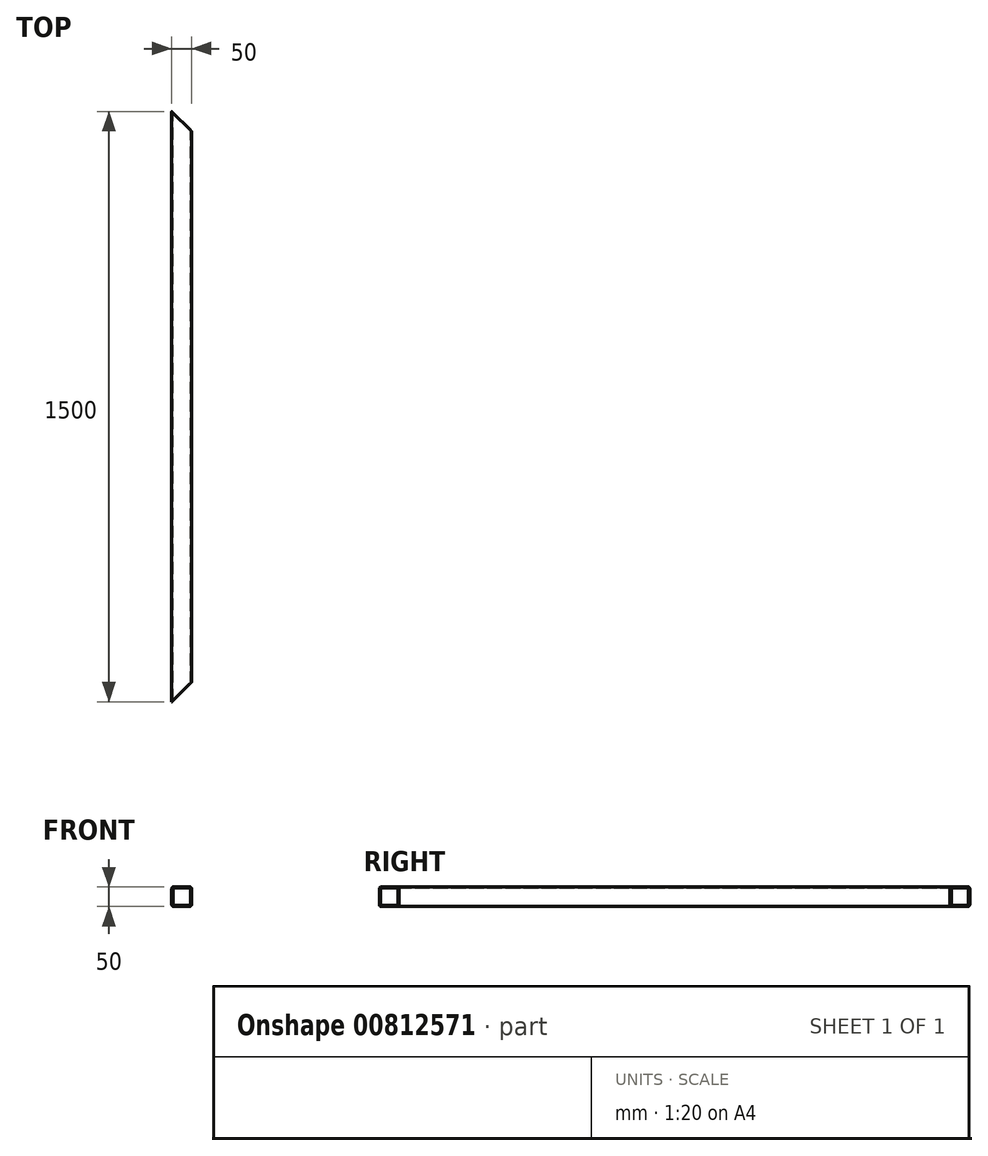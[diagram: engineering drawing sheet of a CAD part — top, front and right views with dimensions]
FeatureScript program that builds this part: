
annotation { "Feature Type Name" : "Feature", "Feature Type Description" : "" }
export const myFeature = defineFeature(function(context is Context, id is Id, definition is map)
    precondition{}
    {
        {
            var Q0;
            Q0=qCreatedBy(makeId("Front.planeOp"),FACE);
            var sketch = newSketch(context, id + "F0", { "sketchPlane" : qUnion([Q0])});
            skLineSegment(sketch, "E0.bottom", {"start": v(50, 50) * mm, "end": v(0, 50) * mm});
            skLineSegment(sketch, "E0.top", {"start": v(50, 0) * mm, "end": v(0, 0) * mm});
            skLineSegment(sketch, "E0.left", {"start": v(50, 50) * mm, "end": v(50, 0) * mm});
            skLineSegment(sketch, "E0.right", {"start": v(0, 50) * mm, "end": v(0, 0) * mm});
            skLineSegment(sketch, "E1.0", {"start": v(47, 3) * mm, "end": v(3, 3) * mm});
            skLineSegment(sketch, "E1.1", {"start": v(47, 47) * mm, "end": v(47, 3) * mm});
            skLineSegment(sketch, "E1.2", {"start": v(47, 47) * mm, "end": v(3, 47) * mm});
            skLineSegment(sketch, "E1.3", {"start": v(3, 47) * mm, "end": v(3, 3) * mm});
            skSolve(sketch);
        }
        {
            var Q0;
            Q0=qSketchRegion(id+"F0",true);
            extrude(context, id + "F1", {"entities" : qUnion([Q0]), "depth" : 1500 * mm, "offsetDistance" : 25 * mm});
        }
        {
            var Q0;
            Q0=qSketchRegion(id+"F0",true);
            extrude(context, id + "F2", {"entities" : qUnion([Q0]), "operationType" : NewBodyOperationType.ADD, "depth" : 100 * mm, "offsetDistance" : 25 * mm});
        }
        {
            var Q0;
            Q0=makeQuery(id+"F1.opExtrude","SWEPT_EDGE",EDGE,{"disambiguationData":[OSD([sQuery(id+"F0.wireOp",EDGE,"E0.bottom"),sQuery(id+"F0.wireOp",EDGE,"E0.left")])]});
            var Q1;
            Q1=makeQuery(id+"F1.opExtrude","SWEPT_EDGE",EDGE,{"disambiguationData":[OSD([sQuery(id+"F0.wireOp",EDGE,"E0.top"),sQuery(id+"F0.wireOp",EDGE,"E0.left")])]});
            var Q2;
            Q2=makeQuery(id+"F1.opExtrude","SWEPT_EDGE",EDGE,{"disambiguationData":[OSD([sQuery(id+"F0.wireOp",EDGE,"E0.top"),sQuery(id+"F0.wireOp",EDGE,"E0.right")])]});
            var Q3;
            Q3=makeQuery(id+"F1.opExtrude","SWEPT_EDGE",EDGE,{"disambiguationData":[OSD([sQuery(id+"F0.wireOp",EDGE,"E0.bottom"),sQuery(id+"F0.wireOp",EDGE,"E0.right")])]});
            fillet(context, id + "F3", {"entities" : qUnion([Q0, Q1, Q2, Q3]), "radius" : 5 * mm, "tangentPropagation" : true, "allowEdgeOverflow" : false});
        }
        {
            var Q0;
            Q0=makeQuery(id+"F1.opExtrude","SWEPT_EDGE",EDGE,{"disambiguationData":[OSD([sQuery(id+"F0.wireOp",EDGE,"E1.1"),sQuery(id+"F0.wireOp",EDGE,"E1.2")])]});
            var Q1;
            Q1=makeQuery(id+"F1.opExtrude","SWEPT_EDGE",EDGE,{"disambiguationData":[OSD([sQuery(id+"F0.wireOp",EDGE,"E1.0"),sQuery(id+"F0.wireOp",EDGE,"E1.3")])]});
            var Q2;
            Q2=makeQuery(id+"F1.opExtrude","SWEPT_EDGE",EDGE,{"disambiguationData":[OSD([sQuery(id+"F0.wireOp",EDGE,"E1.2"),sQuery(id+"F0.wireOp",EDGE,"E1.3")])]});
            var Q3;
            Q3=makeQuery(id+"F1.opExtrude","SWEPT_EDGE",EDGE,{"disambiguationData":[OSD([sQuery(id+"F0.wireOp",EDGE,"E1.0"),sQuery(id+"F0.wireOp",EDGE,"E1.1")])]});
            fillet(context, id + "F4", {"entities" : qUnion([Q0, Q1, Q2, Q3]), "radius" : 3 * mm, "tangentPropagation" : true, "allowEdgeOverflow" : false});
        }
        {
            var Q0;
            Q0=makeQuery(id+"F1.opExtrude","SWEPT_FACE",FACE,{"disambiguationData":[OSD([sQuery(id+"F0.wireOp",EDGE,"E0.bottom")])]});
            var sketch = newSketch(context, id + "F5", { "sketchPlane" : qUnion([Q0])});
            skLineSegment(sketch, "E2", {"start": v(0, 0) * mm, "end": v(50, 0) * mm});
            skLineSegment(sketch, "E3", {"start": v(50, 0) * mm, "end": v(50, -50) * mm});
            skLineSegment(sketch, "E4", {"start": v(50, -50) * mm, "end": v(0, 0) * mm});
            skPoint(sketch, "E5.orphan", {"position": v(5, -750) * mm});
            skLineSegment(sketch, "E6", {"start": v(5, -750) * mm, "end": v(45, -750) * mm, "construction": true});
            skLineSegment(sketch, "E7.MirrorCS", {"start": v(0, -1500) * mm, "end": v(50, -1500) * mm});
            skLineSegment(sketch, "E8.MirrorCS", {"start": v(50, -1500) * mm, "end": v(50, -1450) * mm});
            skLineSegment(sketch, "E9.MirrorCS", {"start": v(50, -1450) * mm, "end": v(0, -1500) * mm});
            skSolve(sketch);
        }
        {
            var Q0;
            Q0 = qSketchRegion(id + "F5", true);
            extrude(context, id + "F6", {"entities" : qUnion([Q0]), "operationType" : NewBodyOperationType.REMOVE, "oppositeDirection" : true, "depth" : 50 * mm, "offsetDistance" : 25 * mm});
        }
    });
